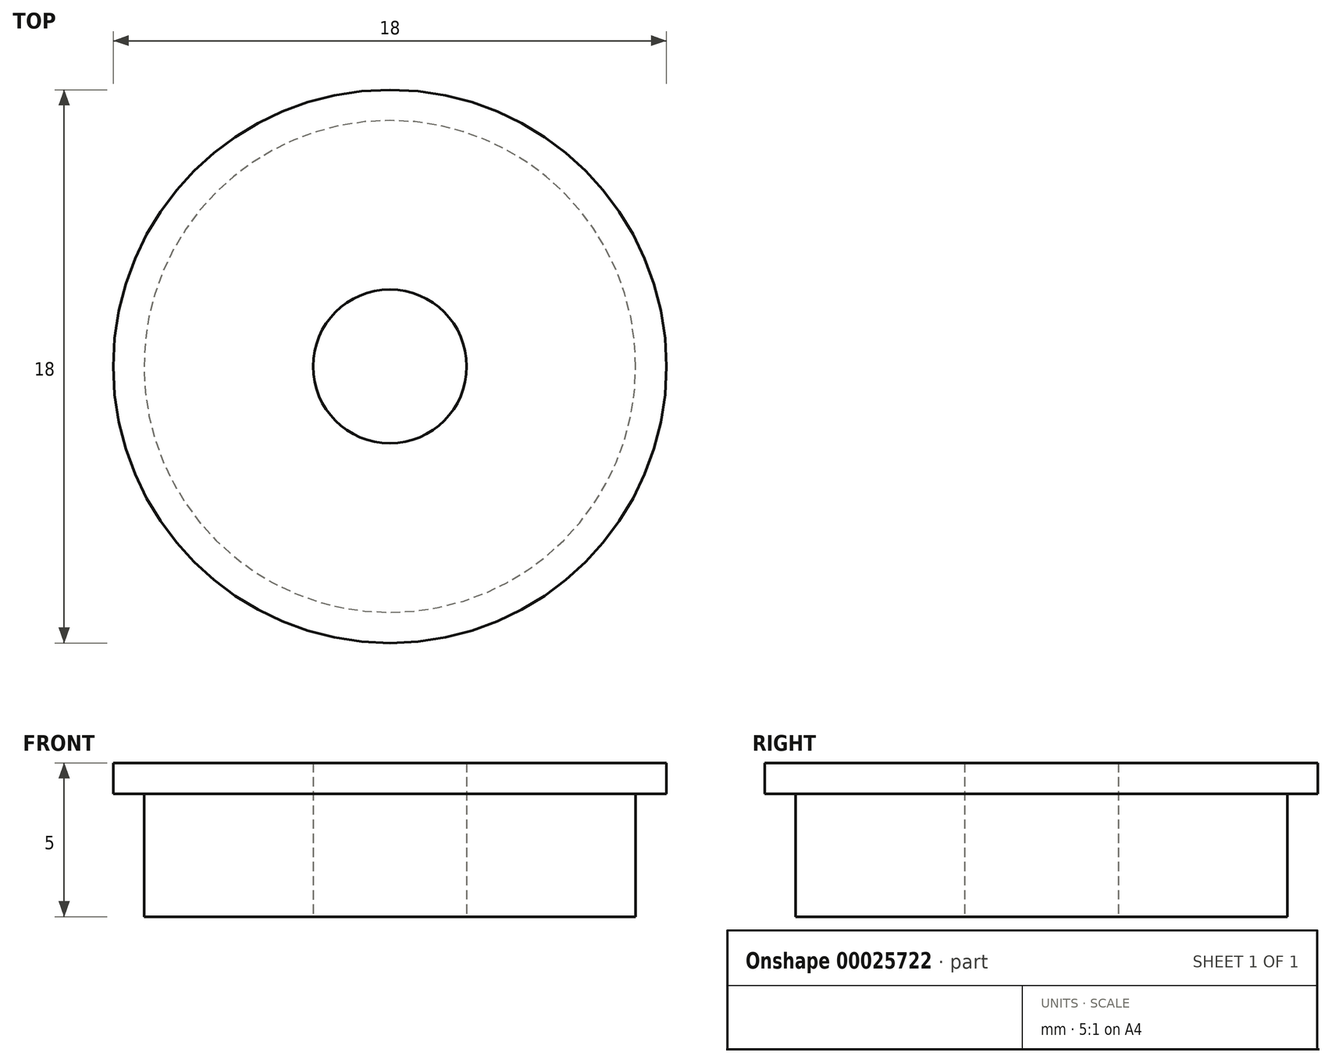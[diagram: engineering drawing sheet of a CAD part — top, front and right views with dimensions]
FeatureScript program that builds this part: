
annotation { "Feature Type Name" : "Feature", "Feature Type Description" : "" }
export const myFeature = defineFeature(function(context is Context, id is Id, definition is map)
    precondition{}
    {
        {
            var Q0;
            Q0=qCreatedBy(makeId("Right.planeOp"),FACE);
            var sketch = newSketch(context, id + "F0", { "sketchPlane" : qUnion([Q0])});
            skLineSegment(sketch, "E0", {"start": v(0, 0) * mm, "end": v(0, 9.32) * mm, "construction": true});
            skLineSegment(sketch, "E1", {"start": v(2.5, 0) * mm, "end": v(2.5, 5) * mm});
            skLineSegment(sketch, "E2", {"start": v(2.5, 5) * mm, "end": v(9, 5) * mm});
            skLineSegment(sketch, "E3", {"start": v(9, 5) * mm, "end": v(9, 4) * mm});
            skLineSegment(sketch, "E4", {"start": v(9, 4) * mm, "end": v(8, 4) * mm});
            skLineSegment(sketch, "E5", {"start": v(8, 4) * mm, "end": v(8, 0) * mm});
            skLineSegment(sketch, "E6", {"start": v(8, 0) * mm, "end": v(2.5, 0) * mm});
            skLineSegment(sketch, "E7", {"start": v(0, 0) * mm, "end": v(2.5, 0) * mm, "construction": true});
            skSolve(sketch);
        }
        {
            var Q0;
            Q0 = qSketchRegion(id + "F0", true);
            var Q1;
            Q1=sQuery(id+"F0.wireOp",EDGE,"E0");
            revolve(context, id + "F1", {"entities" : qUnion([Q0]), "axis" : qUnion([Q1]), "revolveType" : RevolveType.FULL});
        }
    });
